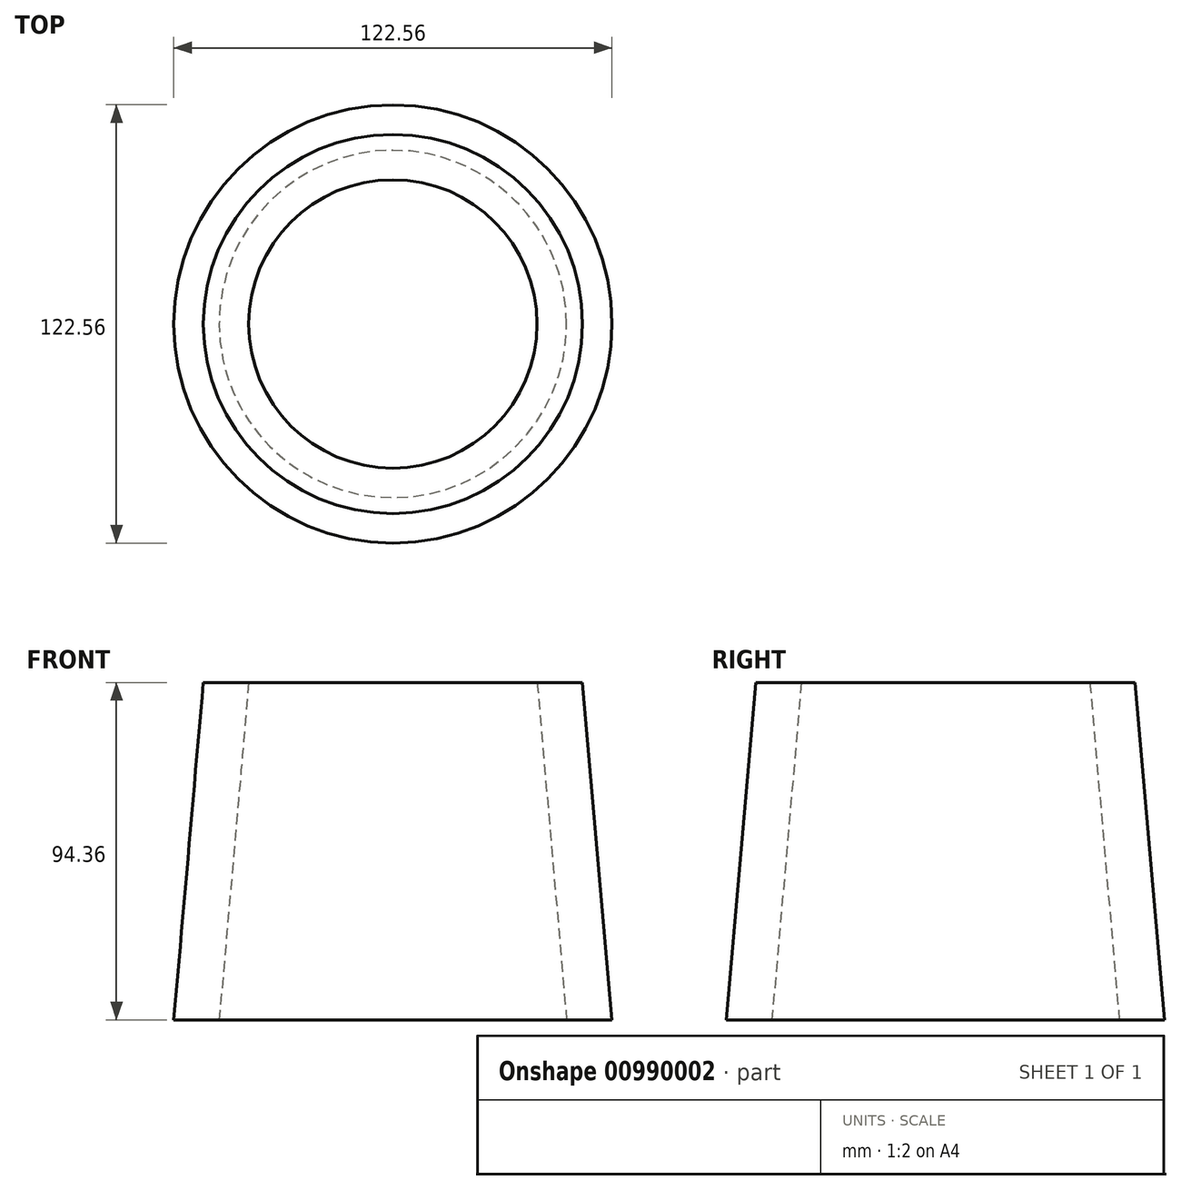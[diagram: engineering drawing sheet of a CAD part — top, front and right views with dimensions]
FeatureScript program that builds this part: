
annotation { "Feature Type Name" : "Feature", "Feature Type Description" : "" }
export const myFeature = defineFeature(function(context is Context, id is Id, definition is map)
    precondition{}
    {
        {
            var Q0;
            Q0=qCreatedBy(makeId("Front.planeOp"),FACE);
            var sketch = newSketch(context, id + "F0", { "sketchPlane" : qUnion([Q0])});
            skLineSegment(sketch, "E0", {"start": v(0, 0) * mm, "end": v(0, 76.2) * mm, "construction": true});
            skLineSegment(sketch, "E1", {"start": v(-61.28, 0) * mm, "end": v(-48.58, 0) * mm});
            skLineSegment(sketch, "E2", {"start": v(-48.58, 0) * mm, "end": v(-40.32, 94.36) * mm});
            skLineSegment(sketch, "E3", {"start": v(-40.32, 94.36) * mm, "end": v(-53.02, 94.36) * mm});
            skLineSegment(sketch, "E4", {"start": v(-53.02, 94.36) * mm, "end": v(-61.28, 0) * mm});
            skSolve(sketch);
        }
        {
            var Q0;
            Q0=makeQuery(id+"F0.imprint","IMPRINT",FACE,{"disambiguationData":[TD([[makeQuery(id+"F0.imprint","IMPRINT",EDGE,{"derivedFrom":sQuery(id+"F0.wireOp",EDGE,"E1")}),1.0]])]});
            var Q1;
            Q1=sQuery(id+"F0.wireOp",EDGE,"E0");
            revolve(context, id + "F1", {"surfaceOperationType" : NewSurfaceOperationType.NEW, "entities" : qUnion([Q0]), "axis" : qUnion([Q1]), "revolveType" : RevolveType.FULL});
        }
    });
